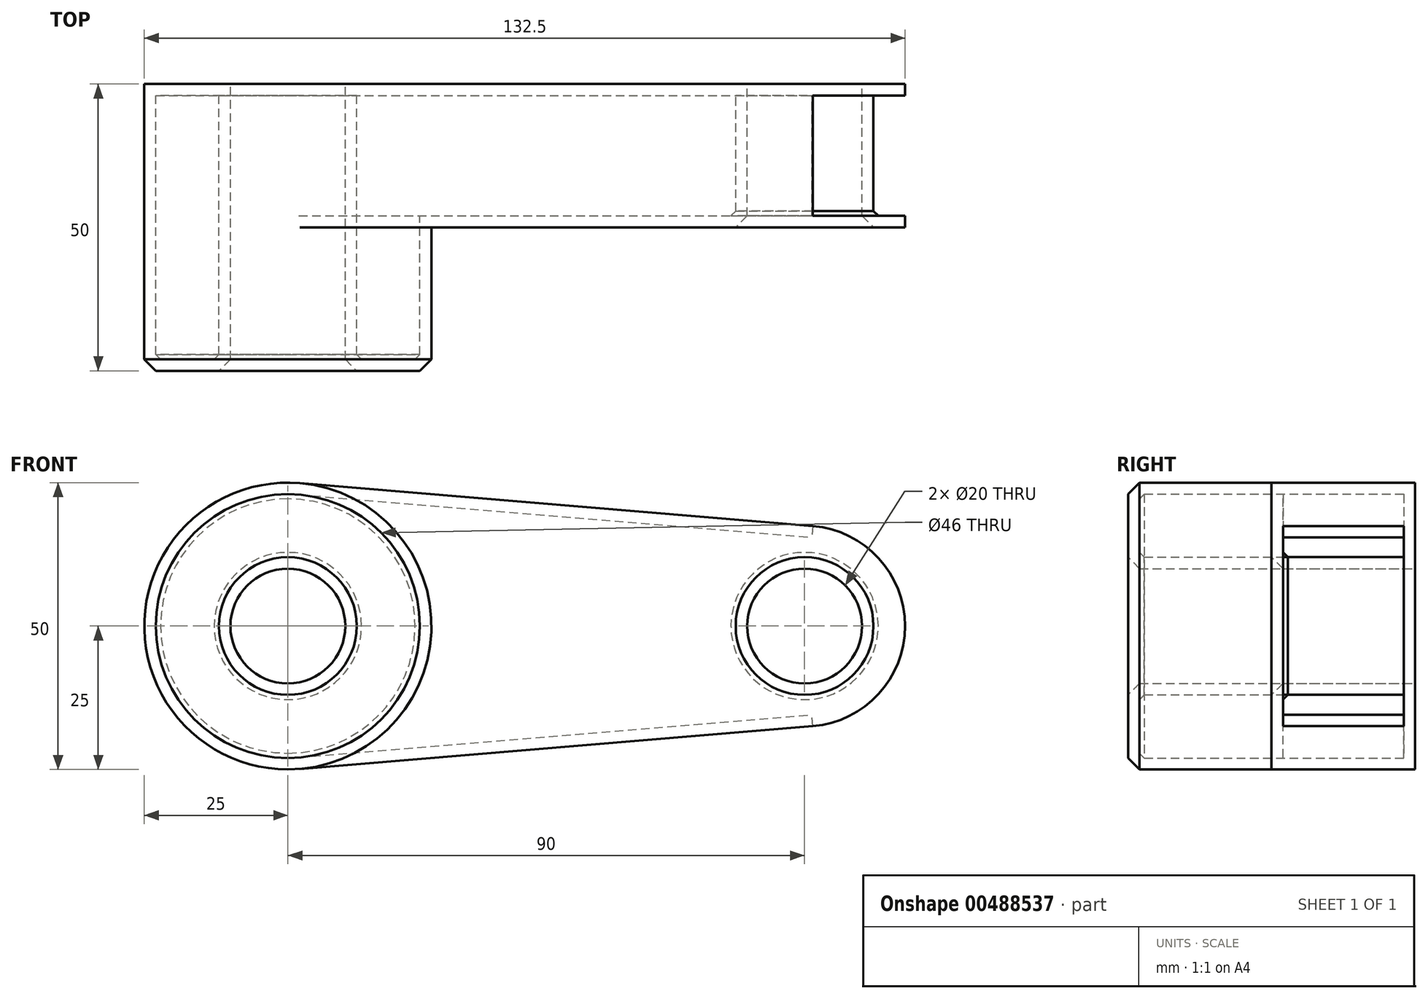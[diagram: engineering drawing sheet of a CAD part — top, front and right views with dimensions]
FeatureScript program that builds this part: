
annotation { "Feature Type Name" : "Feature", "Feature Type Description" : "" }
export const myFeature = defineFeature(function(context is Context, id is Id, definition is map)
    precondition{}
    {
        {
            var Q0;
            Q0=qCreatedBy(makeId("Front.planeOp"),FACE);
            var sketch = newSketch(context, id + "F0", { "sketchPlane" : qUnion([Q0])});
            skCircle(sketch, "E0", {"center": v(0, 0) * mm, "radius": 25 * mm});
            skCircle(sketch, "E1", {"center": v(90, 0) * mm, "radius": 17.5 * mm});
            skLineSegment(sketch, "E2", {"start": v(2.08, 24.91) * mm, "end": v(91.46, 17.44) * mm});
            skLineSegment(sketch, "E3", {"start": v(2.08, -24.91) * mm, "end": v(91.46, -17.44) * mm});
            skCircle(sketch, "E4", {"center": v(0, 0) * mm, "radius": 10 * mm});
            skCircle(sketch, "E5", {"center": v(90, 0) * mm, "radius": 10 * mm});
            skSolve(sketch);
        }
        {
            var Q0;
            Q0=qSketchRegion(id+"F0",true);
            extrude(context, id + "F1", {"entities" : qUnion([Q0]), "depth" : 25 * mm});
        }
        {
            var Q0;
            Q0=makeQuery(id+"F0.imprint","IMPRINT",FACE,{"disambiguationData":[TD([[makeQuery(id+"F0.imprint","IMPRINT",EDGE,{"derivedFrom":sQuery(id+"F0.wireOp",EDGE,"E4")}),-1.0]])]});
            extrude(context, id + "F2", {"entities" : qUnion([Q0]), "operationType" : NewBodyOperationType.ADD, "depth" : 50 * mm});
        }
        {
            var Q0;
            Q0=makeQuery(id+"F2.opExtrude","CAP_EDGE",EDGE,{"disambiguationData":[OSD([sQuery(id+"F0.wireOp",EDGE,"E0")])],"isStart":false});
            var Q1;
            Q1=makeQuery(id+"F2.opExtrude","CAP_EDGE",EDGE,{"disambiguationData":[OSD([sQuery(id+"F0.wireOp",EDGE,"E4")])],"isStart":false});
            var Q2;
            Q2=makeQuery(id+"F1.opExtrude","CAP_EDGE",EDGE,{"disambiguationData":[OSD([sQuery(id+"F0.wireOp",EDGE,"E5")])],"isStart":false});
            chamfer(context, id + "F3", {"entities" : qUnion([Q0, Q1, Q2]), "width" : 2 * mm, "tangentPropagation" : true});
        }
        {
            var Q0;
            Q0=makeQuery(id+"F1.opExtrude","SWEPT_FACE",FACE,{"disambiguationData":[OSD([sQuery(id+"F0.wireOp",EDGE,"E1")])]});
            shell(context, id + "F4", {"entities" : qUnion([Q0]), "thickness" : 2 * mm});
        }
    });
